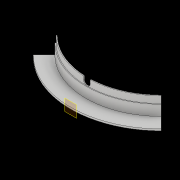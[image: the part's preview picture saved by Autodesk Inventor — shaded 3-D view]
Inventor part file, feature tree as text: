
AUTODESK INVENTOR PART (.ipt)
format: ipt  version: 2017 (Build 210142000, 142)  size: 134,656 bytes
history: native  units: in
note: dims shown in document units (in); Inventor stores cm internally (conversion verified against a paired STEP export)
features: sketch x3, extrude x2, revolve x1, plane x1
ambient origin geometry x8: Origin, YZ Plane, XZ Plane, XY Plane, X Axis, Y Axis, Z Axis, Center Point
bodies: Solid1 (feature_tree)
feature tree (7):
  revolve  "Revolution1"  [1 undecoded]
  plane  "Work Plane2"
  extrude  "Extrusion2"  Depth=0.125in
  extrude  "Extrusion3"  Depth=0.0625in
  sketch  "Sketch1"  dims[d0=2.0in d1=5.4375in]
  sketch  "Sketch3"  dims[d2=1.25in d3=0.125in]
  sketch  "Sketch4"  dims[d4=0.125in d5=2.25in d6=1.5in d7=0.125in d8=90.0deg d13=1.0285in d14=0.0625in d15=0.25in d16=0.25in d17=1.0in d18=0.0in d19=135.0deg d20=90.0deg d21=0.0in d22=0.0in]
note: 1 required parameter value undecoded (feature->parameter linkage not recoverable at this tier; creation-order binding heuristic only, values carry confidence <= 0.55)
